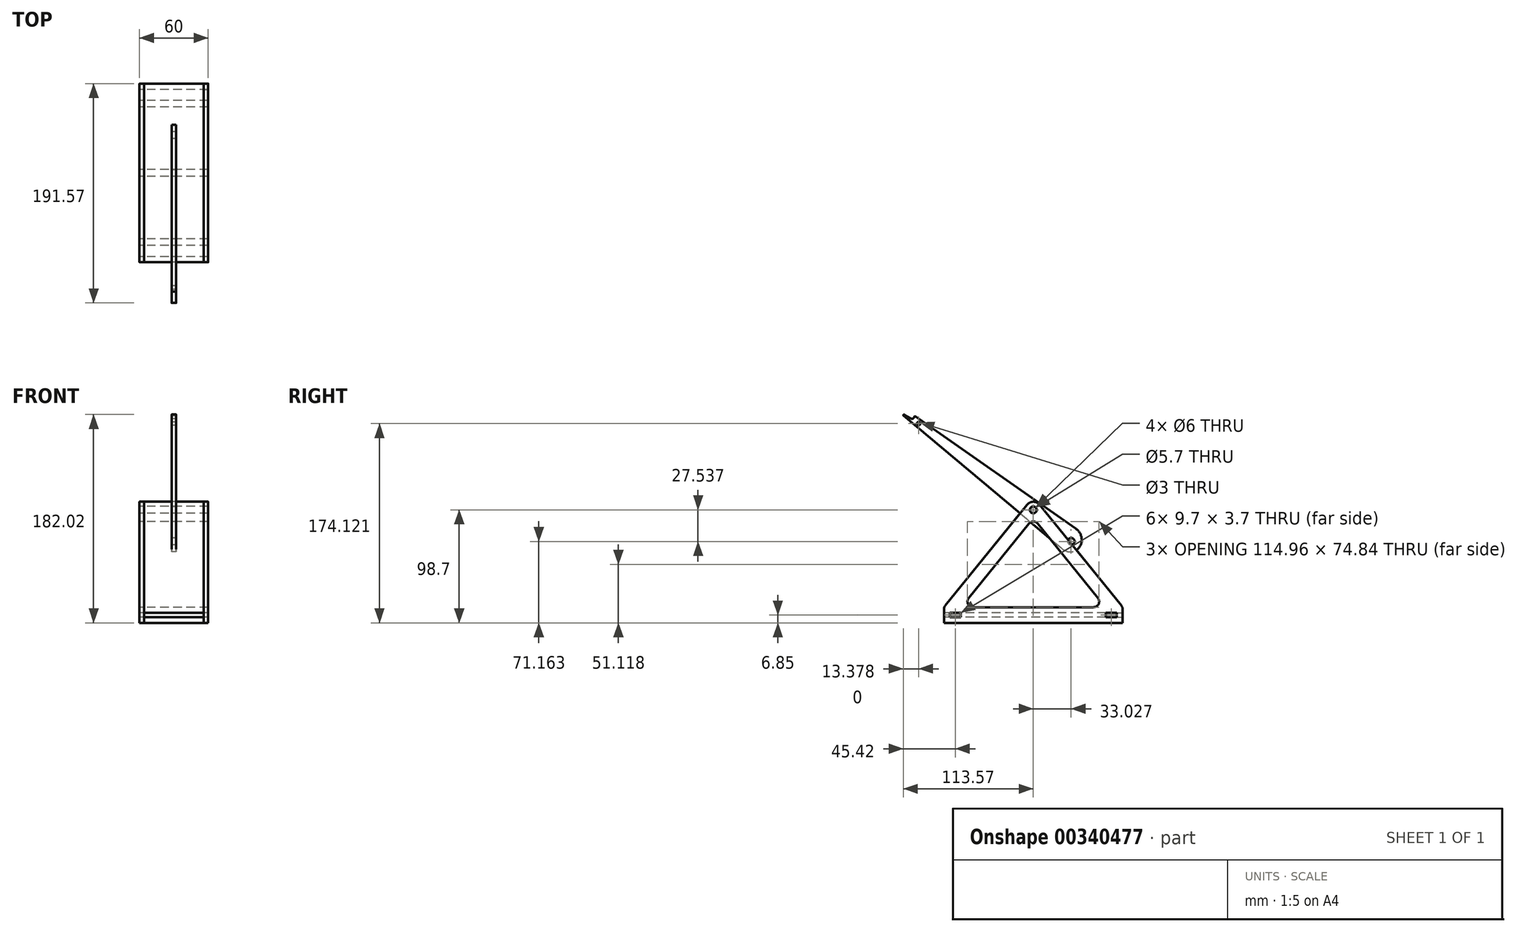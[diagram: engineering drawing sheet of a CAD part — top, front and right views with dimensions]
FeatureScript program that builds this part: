
annotation { "Feature Type Name" : "Feature", "Feature Type Description" : "" }
export const myFeature = defineFeature(function(context is Context, id is Id, definition is map)
    precondition{}
    {
        {
            var Q0;
            Q0=qCreatedBy(makeId("Right.planeOp"),FACE);
            var sketch = newSketch(context, id + "F0", { "sketchPlane" : qUnion([Q0])});
            skLineSegment(sketch, "E0", {"start": v(-3.89, -12.02) * mm, "end": v(-56.4, -76.85) * mm});
            skLineSegment(sketch, "E1", {"start": v(-52.52, -85) * mm, "end": v(0, -85) * mm});
            skLineSegment(sketch, "E2", {"start": v(-76.89, -83.62) * mm, "end": v(-5.53, 4.48) * mm});
            skLineSegment(sketch, "E3", {"start": v(0, -98.7) * mm, "end": v(-78, -98.7) * mm});
            skCircle(sketch, "E4", {"center": v(0, 0) * mm, "radius": 3 * mm});
            skLineSegment(sketch, "E5.bottom", {"start": v(-73, -93.7) * mm, "end": v(-63.3, -93.7) * mm});
            skLineSegment(sketch, "E5.top", {"start": v(-73, -90) * mm, "end": v(-63.3, -90) * mm});
            skLineSegment(sketch, "E5.left", {"start": v(-73, -93.7) * mm, "end": v(-73, -90) * mm});
            skLineSegment(sketch, "E5.right", {"start": v(-63.3, -93.7) * mm, "end": v(-63.3, -90) * mm});
            skLineSegment(sketch, "E6", {"start": v(-78, -98.7) * mm, "end": v(-78, -86.77) * mm});
            skLineSegment(sketch, "E7.MirrorCS", {"start": v(63.3, -93.7) * mm, "end": v(63.3, -90) * mm});
            skLineSegment(sketch, "E8.MirrorCS", {"start": v(73, -93.7) * mm, "end": v(73, -90) * mm});
            skLineSegment(sketch, "E9.MirrorCS", {"start": v(73, -90) * mm, "end": v(63.3, -90) * mm});
            skLineSegment(sketch, "E10.MirrorCS", {"start": v(78, -98.7) * mm, "end": v(78, -86.77) * mm});
            skLineSegment(sketch, "E11.MirrorCS", {"start": v(73, -93.7) * mm, "end": v(63.3, -93.7) * mm});
            skLineSegment(sketch, "E12.MirrorCS", {"start": v(3.89, -12.02) * mm, "end": v(56.4, -76.85) * mm});
            skLineSegment(sketch, "E13.MirrorCS", {"start": v(52.52, -85) * mm, "end": v(0, -85) * mm});
            skLineSegment(sketch, "E14.MirrorCS", {"start": v(0, -98.7) * mm, "end": v(78, -98.7) * mm});
            skLineSegment(sketch, "E15.MirrorCS", {"start": v(76.89, -83.62) * mm, "end": v(5.53, 4.48) * mm});
            skArc(sketch, "E16", {"start": v(5.53, 4.48) * mm, "mid": v(0, 7.11) * mm, "end": v(-5.53, 4.48) * mm});
            skPoint(sketch, "E17.orphan", {"position": v(0, 11.3) * mm});
            skPoint(sketch, "E18.visualSharp", {"position": v(0, -7.22) * mm});
            skArc(sketch, "E18.filletArc", {"start": v(3.89, -12.02) * mm, "mid": v(0, -10.16) * mm, "end": v(-3.89, -12.02) * mm});
            skPoint(sketch, "E19.visualSharp", {"position": v(-63, -85) * mm});
            skArc(sketch, "E19.filletArc", {"start": v(-56.4, -76.85) * mm, "mid": v(-57.03, -82.15) * mm, "end": v(-52.52, -85) * mm});
            skPoint(sketch, "E20.visualSharp", {"position": v(63, -85) * mm});
            skArc(sketch, "E20.filletArc", {"start": v(52.52, -85) * mm, "mid": v(57.03, -82.15) * mm, "end": v(56.4, -76.85) * mm});
            skPoint(sketch, "E21.visualSharp", {"position": v(78, -85) * mm});
            skArc(sketch, "E21.filletArc", {"start": v(78, -86.77) * mm, "mid": v(77.71, -85.1) * mm, "end": v(76.89, -83.62) * mm});
            skPoint(sketch, "E22.visualSharp", {"position": v(-78, -85) * mm});
            skArc(sketch, "E22.filletArc", {"start": v(-76.89, -83.62) * mm, "mid": v(-77.71, -85.1) * mm, "end": v(-78, -86.77) * mm});
            skSolve(sketch);
        }
        {
            var Q0;
            Q0 = qSketchRegion(id + "F0", true);
            extrude(context, id + "F1", {"entities" : qUnion([Q0]), "depth" : 4 * mm});
        }
        {
            var Q0;
            Q0=makeQuery(id+"F1.opExtrude","SWEPT_BODY",BODY,{"disambiguationData":[OSD([sQuery(id+"F0.wireOp",EDGE,"E0"),sQuery(id+"F0.wireOp",EDGE,"E1"),sQuery(id+"F0.wireOp",EDGE,"E2"),sQuery(id+"F0.wireOp",EDGE,"E3"),sQuery(id+"F0.wireOp",EDGE,"E5.bottom"),sQuery(id+"F0.wireOp",EDGE,"E5.top"),sQuery(id+"F0.wireOp",EDGE,"E5.left"),sQuery(id+"F0.wireOp",EDGE,"E5.right"),sQuery(id+"F0.wireOp",EDGE,"E6"),sQuery(id+"F0.wireOp",EDGE,"E7.MirrorCS"),sQuery(id+"F0.wireOp",EDGE,"E8.MirrorCS"),sQuery(id+"F0.wireOp",EDGE,"E9.MirrorCS"),sQuery(id+"F0.wireOp",EDGE,"E10.MirrorCS"),sQuery(id+"F0.wireOp",EDGE,"E4"),sQuery(id+"F0.wireOp",EDGE,"E11.MirrorCS"),sQuery(id+"F0.wireOp",EDGE,"E12.MirrorCS"),sQuery(id+"F0.wireOp",EDGE,"E13.MirrorCS"),sQuery(id+"F0.wireOp",EDGE,"E14.MirrorCS"),sQuery(id+"F0.wireOp",EDGE,"E15.MirrorCS"),sQuery(id+"F0.wireOp",EDGE,"E16"),sQuery(id+"F0.wireOp",EDGE,"E18.filletArc"),sQuery(id+"F0.wireOp",EDGE,"E19.filletArc"),sQuery(id+"F0.wireOp",EDGE,"E20.filletArc"),sQuery(id+"F0.wireOp",EDGE,"E21.filletArc"),sQuery(id+"F0.wireOp",EDGE,"E22.filletArc")])]});
            var Q1;
            Q1=makeQuery(id+"F1.opExtrude","SWEPT_EDGE",EDGE,{"disambiguationData":[OSD([sQuery(id+"F0.wireOp",EDGE,"E3"),sQuery(id+"F0.wireOp",EDGE,"E6")])]});
            transform(context, id + "F2", {"entities" : qUnion([Q0]), "transformType" : TransformType.TRANSLATION_DISTANCE, "transformDirection" : qUnion([Q1]), "distance" : 26 * mm, "oppositeDirection" : true, "makeCopy" : false});
        }
        {
            var Q0;
            Q0=makeQuery(id+"F1.opExtrude","SWEPT_FACE",FACE,{"disambiguationData":[OSD([sQuery(id+"F0.wireOp",EDGE,"E5.top")])]});
            var sketch = newSketch(context, id + "F3", { "sketchPlane" : qUnion([Q0])});
            skLineSegment(sketch, "E23", {"start": v(26, 73) * mm, "end": v(30, 73) * mm});
            skLineSegment(sketch, "E24", {"start": v(30, 73) * mm, "end": v(30, 63.3) * mm});
            skLineSegment(sketch, "E25", {"start": v(30, 63.3) * mm, "end": v(26, 63.3) * mm});
            skLineSegment(sketch, "E26", {"start": v(26, 73) * mm, "end": v(26, 78) * mm});
            skLineSegment(sketch, "E27.MirrorCS", {"start": v(26, -73) * mm, "end": v(30, -73) * mm});
            skLineSegment(sketch, "E28.MirrorCS", {"start": v(30, -63.3) * mm, "end": v(26, -63.3) * mm});
            skLineSegment(sketch, "E29.MirrorCS", {"start": v(26, -73) * mm, "end": v(26, -78) * mm});
            skLineSegment(sketch, "E30.MirrorCS", {"start": v(30, -73) * mm, "end": v(30, -63.3) * mm});
            skLineSegment(sketch, "E31", {"start": v(26, -63.3) * mm, "end": v(26, 63.3) * mm});
            skLineSegment(sketch, "E32.MirrorCS", {"start": v(-26, 73) * mm, "end": v(-30, 73) * mm});
            skLineSegment(sketch, "E33.MirrorCS", {"start": v(-26, -73) * mm, "end": v(-30, -73) * mm});
            skLineSegment(sketch, "E34.MirrorCS", {"start": v(-30, -63.3) * mm, "end": v(-26, -63.3) * mm});
            skLineSegment(sketch, "E35.MirrorCS", {"start": v(-30, 63.3) * mm, "end": v(-26, 63.3) * mm});
            skLineSegment(sketch, "E36.MirrorCS", {"start": v(-26, -73) * mm, "end": v(-26, -78) * mm});
            skLineSegment(sketch, "E37.MirrorCS", {"start": v(-26, 73) * mm, "end": v(-26, 78) * mm});
            skLineSegment(sketch, "E38.MirrorCS", {"start": v(-30, -73) * mm, "end": v(-30, -63.3) * mm});
            skLineSegment(sketch, "E39.MirrorCS", {"start": v(-30, 73) * mm, "end": v(-30, 63.3) * mm});
            skLineSegment(sketch, "E40.MirrorCS", {"start": v(-26, -63.3) * mm, "end": v(-26, 63.3) * mm});
            skLineSegment(sketch, "E41", {"start": v(-26, -78) * mm, "end": v(26, -78) * mm});
            skLineSegment(sketch, "E42", {"start": v(26, 78) * mm, "end": v(-26, 78) * mm});
            skSolve(sketch);
        }
        {
            var Q0;
            Q0 = qSketchRegion(id + "F3", true);
            extrude(context, id + "F4", {"entities" : qUnion([Q0]), "depth" : 3.7 * mm});
        }
        {
            var Q0;
            Q0=makeQuery(id+"F1.opExtrude","SWEPT_BODY",BODY,{"disambiguationData":[OSD([sQuery(id+"F0.wireOp",EDGE,"E0"),sQuery(id+"F0.wireOp",EDGE,"E1"),sQuery(id+"F0.wireOp",EDGE,"E2"),sQuery(id+"F0.wireOp",EDGE,"E3"),sQuery(id+"F0.wireOp",EDGE,"E5.bottom"),sQuery(id+"F0.wireOp",EDGE,"E5.top"),sQuery(id+"F0.wireOp",EDGE,"E5.left"),sQuery(id+"F0.wireOp",EDGE,"E5.right"),sQuery(id+"F0.wireOp",EDGE,"E6"),sQuery(id+"F0.wireOp",EDGE,"E7.MirrorCS"),sQuery(id+"F0.wireOp",EDGE,"E8.MirrorCS"),sQuery(id+"F0.wireOp",EDGE,"E9.MirrorCS"),sQuery(id+"F0.wireOp",EDGE,"E10.MirrorCS"),sQuery(id+"F0.wireOp",EDGE,"E4"),sQuery(id+"F0.wireOp",EDGE,"E11.MirrorCS"),sQuery(id+"F0.wireOp",EDGE,"E12.MirrorCS"),sQuery(id+"F0.wireOp",EDGE,"E13.MirrorCS"),sQuery(id+"F0.wireOp",EDGE,"E14.MirrorCS"),sQuery(id+"F0.wireOp",EDGE,"E15.MirrorCS"),sQuery(id+"F0.wireOp",EDGE,"E16"),sQuery(id+"F0.wireOp",EDGE,"E18.filletArc"),sQuery(id+"F0.wireOp",EDGE,"E19.filletArc"),sQuery(id+"F0.wireOp",EDGE,"E20.filletArc"),sQuery(id+"F0.wireOp",EDGE,"E21.filletArc"),sQuery(id+"F0.wireOp",EDGE,"E22.filletArc")])]});
            var Q1;
            Q1=makeQuery(id+"F4.opExtrude","CAP_EDGE",EDGE,{"disambiguationData":[OSD([sQuery(id+"F3.wireOp",EDGE,"E42")])],"isStart":true});
            transform(context, id + "F5", {"entities" : qUnion([Q0]), "transformType" : TransformType.TRANSLATION_DISTANCE, "transformDirection" : qUnion([Q1]), "distance" : 56 * mm, "makeCopy" : true});
        }
        {
            var Q0;
            Q0=makeQuery(id+"F0.imprint","IMPRINT",FACE,{"disambiguationData":[TD([[makeQuery(id+"F0.imprint","IMPRINT",EDGE,{"derivedFrom":sQuery(id+"F0.wireOp",EDGE,"E4")}),-1.0]])]});
            extrude(context, id + "F6", {"entities" : qUnion([Q0]), "depth" : 30 * mm, "hasSecondDirection" : true, "secondDirectionOppositeDirection" : true, "secondDirectionDepth" : 30 * mm});
        }
        {
            var Q0;
            Q0=qCreatedBy(makeId("Right.planeOp"),FACE);
            var sketch = newSketch(context, id + "F7", { "sketchPlane" : qUnion([Q0])});
            skLineSegment(sketch, "E43", {"start": v(133.35, 7.67) * mm, "end": v(139.96, 8.73) * mm});
            skLineSegment(sketch, "E44", {"start": v(140.2, 9.01) * mm, "end": v(140.23, 9.43) * mm});
            skLineSegment(sketch, "E45", {"start": v(139.93, 9.75) * mm, "end": v(-41.71, 9.75) * mm});
            skCircle(sketch, "E46", {"center": v(0, 0) * mm, "radius": 2.85 * mm});
            skCircle(sketch, "E47", {"center": v(-43, -0.13) * mm, "radius": 3 * mm});
            skArc(sketch, "E48.filletArc", {"start": v(140.23, 9.43) * mm, "mid": v(140.15, 9.65) * mm, "end": v(139.93, 9.75) * mm});
            skArc(sketch, "E49", {"start": v(133.35, 7.67) * mm, "mid": v(132.15, 7.02) * mm, "end": v(131.63, 5.76) * mm});
            skArc(sketch, "E50", {"start": v(131.63, 5.76) * mm, "mid": v(131.78, 4.68) * mm, "end": v(132.3, 3.72) * mm});
            skPoint(sketch, "E51.visualSharp", {"position": v(140.2, 8.77) * mm});
            skArc(sketch, "E51.filletArc", {"start": v(139.96, 8.73) * mm, "mid": v(140.13, 8.83) * mm, "end": v(140.2, 9.01) * mm});
            skLineSegment(sketch, "E52", {"start": v(-38.93, -11.36) * mm, "end": v(132.3, 3.72) * mm});
            skCircle(sketch, "E53", {"center": v(125.23, 6.63) * mm, "radius": 1.5 * mm});
            skArc(sketch, "E54", {"start": v(-41.71, 9.75) * mm, "mid": v(-42.76, 9.7) * mm, "end": v(-43.8, 9.54) * mm});
            skPoint(sketch, "E55.visualSharp", {"position": v(-52.37, 0) * mm});
            skArc(sketch, "E55.filletArc", {"start": v(-43.8, 9.54) * mm, "mid": v(-51.23, 3.2) * mm, "end": v(-49.72, -6.44) * mm});
            skLineSegment(sketch, "E56", {"start": v(-49.72, -6.44) * mm, "end": v(-49.43, -6.8) * mm});
            skPoint(sketch, "E57.orphan", {"position": v(-38.46, -11.32) * mm});
            skPoint(sketch, "E58.visualSharp", {"position": v(-45.42, -11.93) * mm});
            skArc(sketch, "E58.filletArc", {"start": v(-49.43, -6.8) * mm, "mid": v(-44.76, -10.42) * mm, "end": v(-38.93, -11.36) * mm});
            skSolve(sketch);
        }
        {
            var Q0;
            Q0 = qSketchRegion(id + "F7", true);
            extrude(context, id + "F8", {"entities" : qUnion([Q0]), "depth" : 2 * mm, "hasSecondDirection" : true, "secondDirectionOppositeDirection" : true, "secondDirectionDepth" : 2 * mm});
        }
        {
            var Q0;
            Q0=makeQuery(id+"F8.opExtrude","SWEPT_BODY",BODY,{"disambiguationData":[OSD([sQuery(id+"F7.wireOp",EDGE,"E43"),sQuery(id+"F7.wireOp",EDGE,"E44"),sQuery(id+"F7.wireOp",EDGE,"e69f2c47-12bb-4d9a-ba00-eff30756152d"),sQuery(id+"F7.wireOp",EDGE,"eaf19add-6f64-4571-8da7-e6cb6a6e360b.filletArc"),sQuery(id+"F7.wireOp",EDGE,"E45"),sQuery(id+"F7.wireOp",EDGE,"E46"),sQuery(id+"F7.wireOp",EDGE,"E47"),sQuery(id+"F7.wireOp",EDGE,"E48.filletArc"),sQuery(id+"F7.wireOp",EDGE,"E49"),sQuery(id+"F7.wireOp",EDGE,"E50"),sQuery(id+"F7.wireOp",EDGE,"E51.filletArc"),sQuery(id+"F7.wireOp",EDGE,"E52"),sQuery(id+"F7.wireOp",EDGE,"E53")])]});
            var Q1;
            Q1=makeQuery(id+"F6.opExtrude","SWEPT_FACE",FACE,{"disambiguationData":[OSD([sQuery(id+"F0.wireOp",EDGE,"E4")])]});
            transform(context, id + "F9", {"entities" : qUnion([Q0]), "transformType" : TransformType.ROTATION, "transformAxis" : qUnion([Q1]), "angle" : 140 * degree, "makeCopy" : false});
        }
    });
